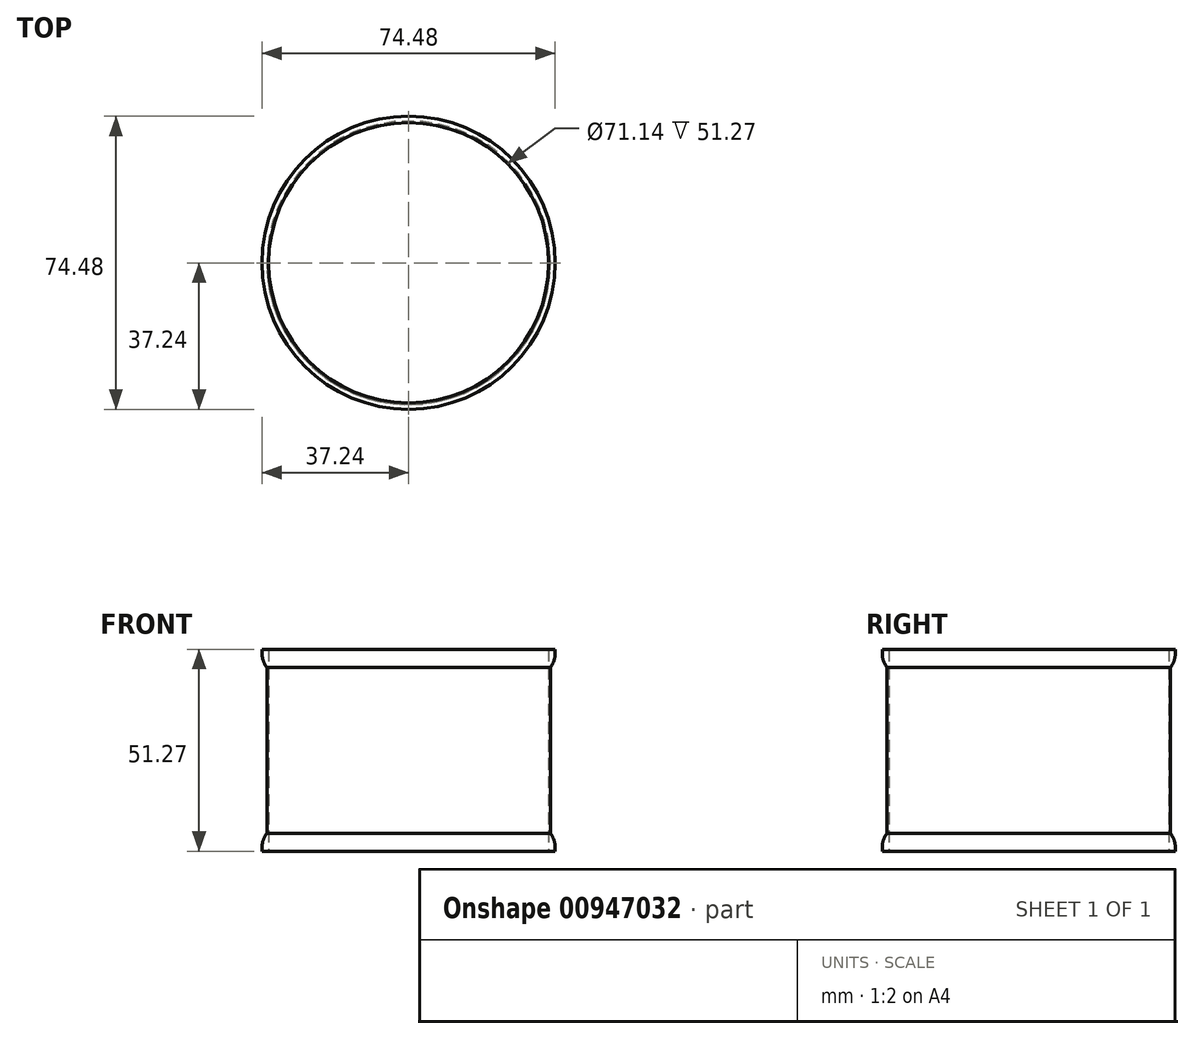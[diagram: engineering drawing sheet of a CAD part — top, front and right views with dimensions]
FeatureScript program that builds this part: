
annotation { "Feature Type Name" : "Feature", "Feature Type Description" : "" }
export const myFeature = defineFeature(function(context is Context, id is Id, definition is map)
    precondition{}
    {
        {
            var Q0;
            Q0=qCreatedBy(makeId("Top.planeOp"),FACE);
            var sketch = newSketch(context, id + "F0", { "sketchPlane" : qUnion([Q0])});
            skCircle(sketch, "E0", {"center": v(0, 0) * mm, "radius": 37.23 * mm});
            skCircle(sketch, "E1", {"center": v(0, 0) * mm, "radius": 35.57 * mm});
            skSolve(sketch);
        }
        {
            var Q0;
            Q0 = qSketchRegion(id + "F0", true);
            extrude(context, id + "F1", {"entities" : qUnion([Q0]), "depth" : 4.6 * mm, "offsetDistance" : 25 * mm});
        }
        {
            var Q0;
            Q0=makeQuery(id+"F1.opExtrude","CAP_FACE",FACE,{"disambiguationData":[OSD([sQuery(id+"F0.wireOp",EDGE,"E0")])],"isStart":false});
            var sketch = newSketch(context, id + "F2", { "sketchPlane" : qUnion([Q0])});
            skCircle(sketch, "E2", {"center": v(0, 0) * mm, "radius": 36 * mm});
            skCircle(sketch, "E3", {"center": v(0, 0) * mm, "radius": 35.57 * mm});
            skSolve(sketch);
        }
        {
            var Q0;
            Q0 = qSketchRegion(id + "F2", true);
            extrude(context, id + "F3", {"entities" : qUnion([Q0]), "operationType" : NewBodyOperationType.ADD, "depth" : 42.07 * mm, "offsetDistance" : 25 * mm});
        }
        {
            var Q0;
            Q0=makeQuery(id+"F3.opExtrude","CAP_FACE",FACE,{"disambiguationData":[OSD([sQuery(id+"F2.wireOp",EDGE,"E2")])],"isStart":false});
            var sketch = newSketch(context, id + "F4", { "sketchPlane" : qUnion([Q0])});
            skCircle(sketch, "E4", {"center": v(0, 0) * mm, "radius": 37.23 * mm});
            skCircle(sketch, "E5", {"center": v(0, 0) * mm, "radius": 35.57 * mm});
            skSolve(sketch);
        }
        {
            var Q0;
            Q0 = qSketchRegion(id + "F4", true);
            extrude(context, id + "F5", {"entities" : qUnion([Q0]), "operationType" : NewBodyOperationType.ADD, "depth" : 4.6 * mm, "offsetDistance" : 25 * mm});
        }
        {
            var Q0;
            Q0=makeQuery(id+"F1.opExtrude","CAP_EDGE",EDGE,{"disambiguationData":[OSD([sQuery(id+"F0.wireOp",EDGE,"E0")])],"isStart":false});
            var Q1;
            Q1=makeQuery(id+"F5.opExtrude","CAP_EDGE",EDGE,{"disambiguationData":[OSD([sQuery(id+"F4.wireOp",EDGE,"E4")])],"isStart":true});
            fillet(context, id + "F6", {"entities" : qUnion([Q0, Q1]), "radius" : 6.04 * mm, "tangentPropagation" : true, "allowEdgeOverflow" : false});
        }
    });
